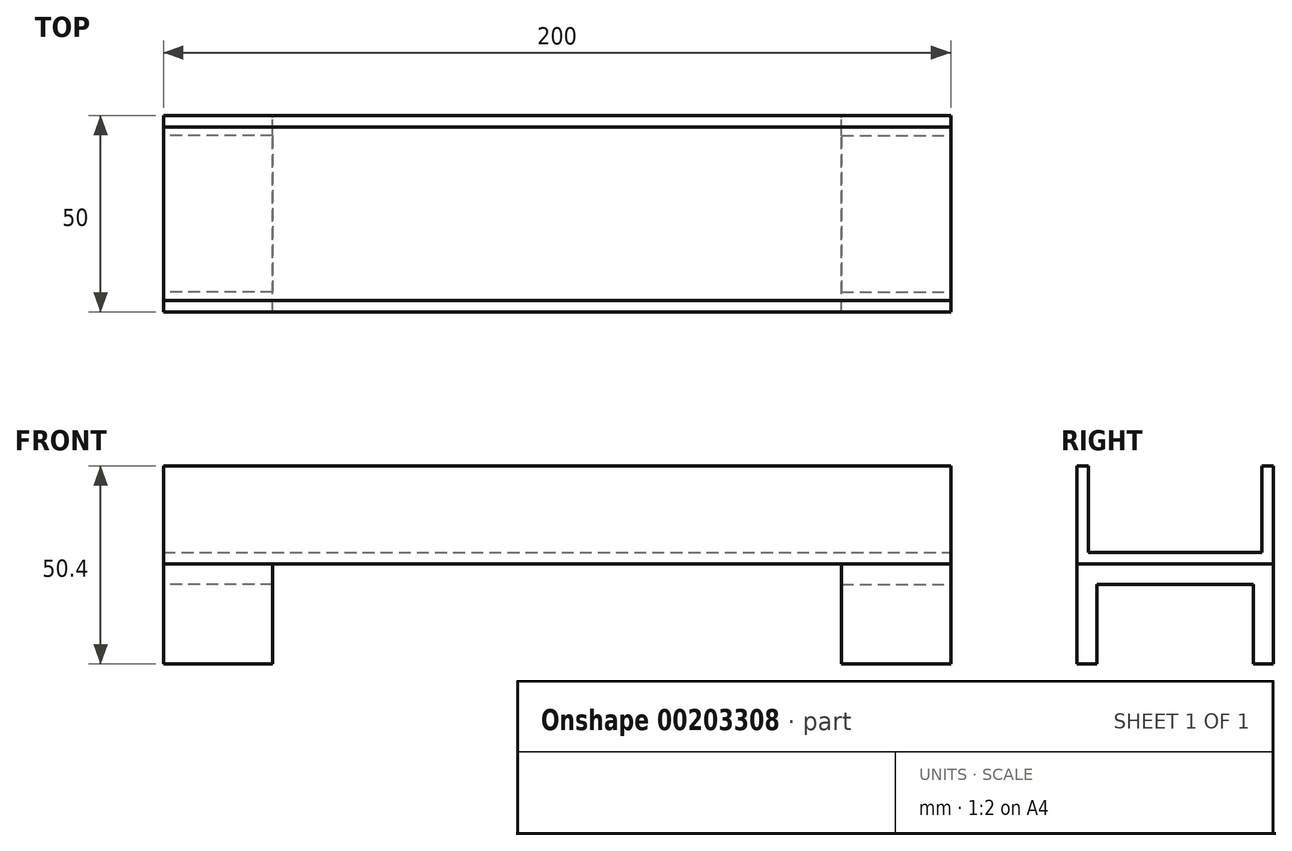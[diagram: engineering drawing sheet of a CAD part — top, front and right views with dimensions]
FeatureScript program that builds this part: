
annotation { "Feature Type Name" : "Feature", "Feature Type Description" : "" }
export const myFeature = defineFeature(function(context is Context, id is Id, definition is map)
    precondition{}
    {
        {
            var Q0;
            Q0=qCreatedBy(makeId("Front.planeOp"),FACE);
            var sketch = newSketch(context, id + "F0", { "sketchPlane" : qUnion([Q0])});
            skLineSegment(sketch, "E0.bottom", {"start": v(100, 12.5) * mm, "end": v(-100, 12.5) * mm});
            skLineSegment(sketch, "E0.top", {"start": v(100, -12.5) * mm, "end": v(-100, -12.5) * mm});
            skLineSegment(sketch, "E0.left", {"start": v(100, 12.5) * mm, "end": v(100, -12.5) * mm});
            skLineSegment(sketch, "E0.right", {"start": v(-100, 12.5) * mm, "end": v(-100, -12.5) * mm});
            skPoint(sketch, "E0.middle", {"position": v(0, 0) * mm});
            skSolve(sketch);
        }
        {
            var Q0;
            Q0=makeQuery(id+"F0.imprint","IMPRINT",FACE,{"disambiguationData":[TD([[makeQuery(id+"F0.imprint","IMPRINT",EDGE,{"derivedFrom":sQuery(id+"F0.wireOp",EDGE,"E0.bottom")}),1.0]])]});
            extrude(context, id + "F1", {"entities" : qUnion([Q0]), "depth" : 50 * mm});
        }
        {
            var Q0;
            Q0=makeQuery(id+"F1.opExtrude","SWEPT_FACE",FACE,{"disambiguationData":[OSD([sQuery(id+"F0.wireOp",EDGE,"E0.left")])]});
            var sketch = newSketch(context, id + "F2", { "sketchPlane" : qUnion([Q0])});
            skLineSegment(sketch, "E1.bottom", {"start": v(-47, 12.5) * mm, "end": v(-3, 12.5) * mm});
            skLineSegment(sketch, "E1.top", {"start": v(-47, -9.5) * mm, "end": v(-3, -9.5) * mm});
            skLineSegment(sketch, "E1.left", {"start": v(-47, 12.5) * mm, "end": v(-47, -9.5) * mm});
            skLineSegment(sketch, "E1.right", {"start": v(-3, 12.5) * mm, "end": v(-3, -9.5) * mm});
            skLineSegment(sketch, "E2", {"start": v(-50, 5.44) * mm, "end": v(-47, 5.44) * mm, "construction": true});
            skLineSegment(sketch, "E3", {"start": v(-23, -12.5) * mm, "end": v(-23, -9.5) * mm, "construction": true});
            skLineSegment(sketch, "E4", {"start": v(0, 5.44) * mm, "end": v(-3, 5.44) * mm, "construction": true});
            skSolve(sketch);
        }
        {
            var Q0;
            Q0 = qSketchRegion(id + "F2", true);
            extrude(context, id + "F3", {"entities" : qUnion([Q0]), "operationType" : NewBodyOperationType.REMOVE, "endBound" : BoundingType.THROUGH_ALL, "oppositeDirection" : true, "depth" : 25.4 * mm});
        }
        {
            var Q0;
            Q0=makeQuery(id+"F1.opExtrude","SWEPT_FACE",FACE,{"disambiguationData":[OSD([sQuery(id+"F0.wireOp",EDGE,"E0.top")])]});
            var sketch = newSketch(context, id + "F4", { "sketchPlane" : qUnion([Q0])});
            skLineSegment(sketch, "E5.bottom", {"start": v(-72.3, 50) * mm, "end": v(-100, 50) * mm});
            skLineSegment(sketch, "E5.top", {"start": v(-72.3, 0) * mm, "end": v(-100, 0) * mm});
            skLineSegment(sketch, "E5.left", {"start": v(-72.3, 50) * mm, "end": v(-72.3, 0) * mm});
            skLineSegment(sketch, "E5.right", {"start": v(-100, 50) * mm, "end": v(-100, 0) * mm});
            skSolve(sketch);
        }
        {
            var Q0;
            Q0=makeQuery(id+"F4.imprint","IMPRINT",FACE,{"disambiguationData":[TD([[makeQuery(id+"F4.imprint","IMPRINT",EDGE,{"derivedFrom":sQuery(id+"F4.wireOp",EDGE,"E5.bottom")}),1.0]])]});
            extrude(context, id + "F5", {"entities" : qUnion([Q0]), "depth" : 25.4 * mm});
        }
        {
            var Q0;
            Q0=makeQuery(id+"F5.opExtrude","SWEPT_FACE",FACE,{"disambiguationData":[OSD([sQuery(id+"F4.wireOp",EDGE,"E5.right")])]});
            var sketch = newSketch(context, id + "F6", { "sketchPlane" : qUnion([Q0])});
            skLineSegment(sketch, "E6.bottom", {"start": v(44.84, -37.9) * mm, "end": v(5.16, -37.9) * mm});
            skLineSegment(sketch, "E6.top", {"start": v(44.84, -17.66) * mm, "end": v(5.16, -17.66) * mm});
            skLineSegment(sketch, "E6.left", {"start": v(44.84, -37.9) * mm, "end": v(44.84, -17.66) * mm});
            skLineSegment(sketch, "E6.right", {"start": v(5.16, -37.9) * mm, "end": v(5.16, -17.66) * mm});
            skLineSegment(sketch, "E7", {"start": v(0, -25.2) * mm, "end": v(5.16, -25.2) * mm, "construction": true});
            skLineSegment(sketch, "E8", {"start": v(22.5, -12.5) * mm, "end": v(22.5, -17.66) * mm, "construction": true});
            skLineSegment(sketch, "E9", {"start": v(50, -25.2) * mm, "end": v(44.84, -25.2) * mm, "construction": true});
            skSolve(sketch);
        }
        {
            var Q0;
            Q0 = qSketchRegion(id + "F6", true);
            extrude(context, id + "F7", {"entities" : qUnion([Q0]), "operationType" : NewBodyOperationType.REMOVE, "endBound" : BoundingType.THROUGH_ALL, "oppositeDirection" : true, "depth" : 25.4 * mm});
        }
        {
            var Q0;
            Q0=makeQuery(id+"F5.opExtrude","SWEPT_BODY",BODY,{"disambiguationData":[OSD([sQuery(id+"F4.wireOp",EDGE,"E5.bottom"),sQuery(id+"F4.wireOp",EDGE,"E5.top"),sQuery(id+"F4.wireOp",EDGE,"E5.left"),sQuery(id+"F4.wireOp",EDGE,"E5.right")])]});
            var Q1;
            Q1=qCreatedBy(makeId("Right.planeOp"),FACE);
            mirror(context, id + "F8", {"entities" : qUnion([Q0]), "mirrorPlane" : qUnion([Q1])});
        }
    });
